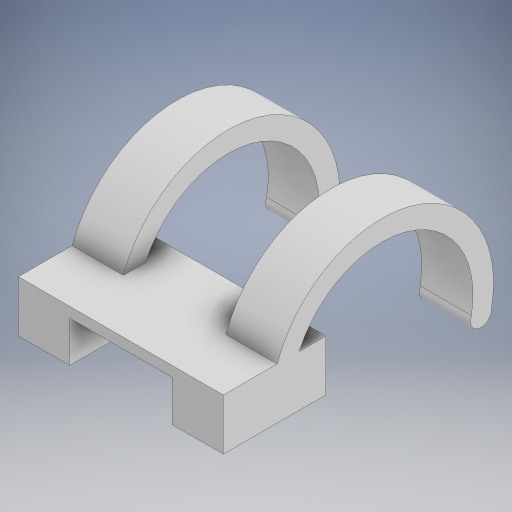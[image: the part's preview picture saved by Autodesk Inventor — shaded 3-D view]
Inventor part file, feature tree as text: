
AUTODESK INVENTOR PART (.ipt)
format: ipt  version: 2024.2 (Build 282272000, 272)  size: 287,232 bytes
history: native  units: in
note: dims shown in document units (in); Inventor stores cm internally (conversion verified against a paired STEP export)
features: extrude x2, sketch x2, plane x1, mirror x1
ambient origin geometry x8: Origin, YZ Plane, XZ Plane, XY Plane, X Axis, Y Axis, Z Axis, Center Point
bodies: Body1 (feature_tree)
feature tree (6):
  extrude  "Extrusion2"  Depth=1.0in
  plane  "Work Plane1"
  mirror  "Mirror1"
  extrude  "Extrusion3"  Depth=0.5in TaperAngle=0.0deg
  sketch  "Sketch2"  dims[d4=0.5in d5=1.0in]
  sketch  "Sketch3"  dims[d6=0.2in d7=0.5in d8=0.0in d9=0.5in d10=0.1in d11=0.5in d12=0.0in]
